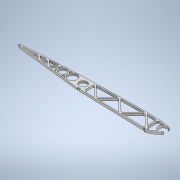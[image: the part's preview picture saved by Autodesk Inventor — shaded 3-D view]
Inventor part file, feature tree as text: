
AUTODESK INVENTOR PART (.ipt)
format: ipt  version: 2022 (Build 260153000, 153)  size: 445,440 bytes
history: native  units: mm
features: extrude x1, sketch x1
ambient origin geometry x8: Origin, YZ Plane, XZ Plane, XY Plane, X Axis, Y Axis, Z Axis, Center Point
bodies: Body1 (feature_tree)
feature tree (2):
  extrude  "Extrusion5"  Depth=10.0mm
  sketch  "Sketch1"  dims[d31=34.456mm d50=368.759386mm d57=16.0mm d69=8.0mm d70=23.0mm d71=8.0mm d73=16.0mm d80=19.0mm d81=16.0mm d82=1.0mm d83=1.0mm d84=1.0mm d85=1.0mm d86=1.0mm d87=0.8mm d88=1.0mm d90=19.0mm d94=5.0mm d95=5.0mm d105=5.0mm d106=5.0mm d108=2.0mm d109=19.0mm d114=5.0mm d115=5.0mm d116=24.0mm d117=2.5mm d118=2.5mm d123=2.5mm d124=2.5mm d125=10.0mm d126=24.0mm d127=24.0mm d128=27.0mm d135=0.5mm d136=45.0deg d139=7.0mm d165=45.0deg d169=27.0mm d175=90.0deg d181=45.0deg d185=7.0mm d186=45.0deg d190=7.0mm d191=45.0deg d197=90.0deg d203=90.0deg d206=7.0mm d207=5.0mm d208=0.0mm]
